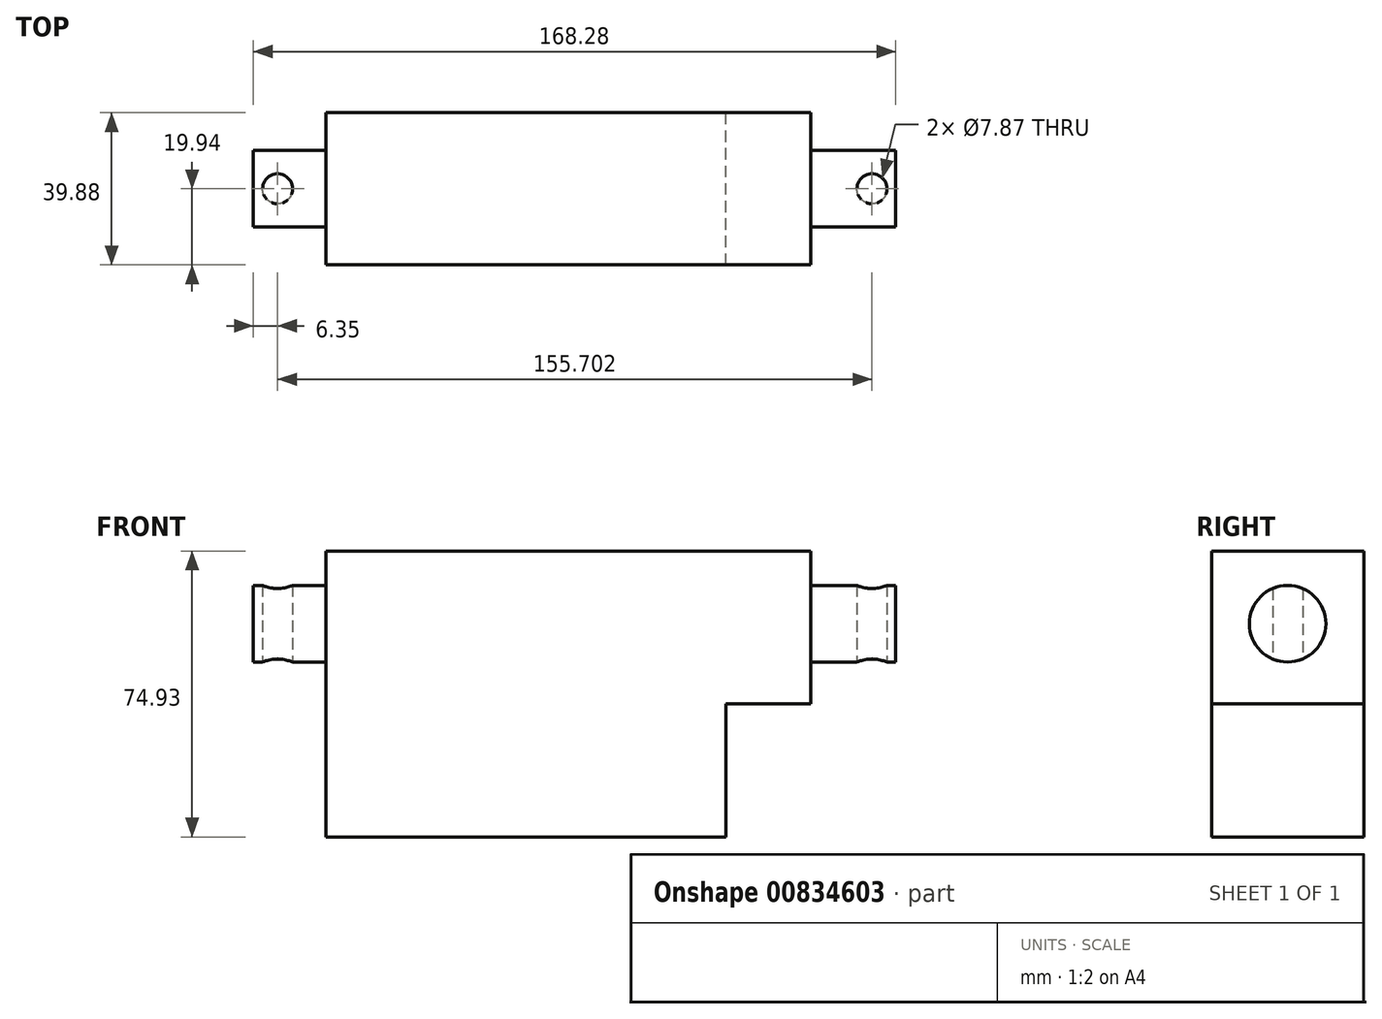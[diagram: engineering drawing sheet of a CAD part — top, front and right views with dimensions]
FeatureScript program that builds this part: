
annotation { "Feature Type Name" : "Feature", "Feature Type Description" : "" }
export const myFeature = defineFeature(function(context is Context, id is Id, definition is map)
    precondition{}
    {
        {
            var Q0;
            Q0=qCreatedBy(makeId("Right.planeOp"),FACE);
            var sketch = newSketch(context, id + "F0", { "sketchPlane" : qUnion([Q0])});
            skCircle(sketch, "E0", {"center": v(0, 0) * mm, "radius": 10.03 * mm});
            skSolve(sketch);
        }
        {
            var Q0;
            Q0 = qSketchRegion(id + "F0", true);
            extrude(context, id + "F1", {"entities" : qUnion([Q0]), "depth" : 168.27 * mm, "offsetDistance" : 25.4 * mm});
        }
        {
            var Q0;
            Q0=qCreatedBy(makeId("Right.planeOp"),FACE);
            cPlane(context, id + "F2", {"entities" : qUnion([Q0]), "cplaneType" : CPlaneType.OFFSET, "offset" : 19.05 * mm, "width" : 152.4 * mm, "height" : 152.4 * mm});
        }
        {
            var Q0;
            Q0=qCreatedBy(id+"F2.planeOp",FACE);
            var sketch = newSketch(context, id + "F3", { "sketchPlane" : qUnion([Q0])});
            skLineSegment(sketch, "E1.bottom", {"start": v(-19.94, 19.05) * mm, "end": v(19.94, 19.05) * mm});
            skLineSegment(sketch, "E1.top", {"start": v(-19.94, -55.88) * mm, "end": v(19.94, -55.88) * mm});
            skLineSegment(sketch, "E1.left", {"start": v(-19.94, 19.05) * mm, "end": v(-19.94, -55.88) * mm});
            skLineSegment(sketch, "E1.right", {"start": v(19.94, 19.05) * mm, "end": v(19.94, -55.88) * mm});
            skSolve(sketch);
        }
        {
            var Q0;
            Q0=makeQuery(id+"F3.imprint","IMPRINT",FACE,{"disambiguationData":[TD([[makeQuery(id+"F3.imprint","IMPRINT",EDGE,{"derivedFrom":sQuery(id+"F3.wireOp",EDGE,"E1.bottom")}),-1.0]])]});
            extrude(context, id + "F4", {"entities" : qUnion([Q0]), "operationType" : NewBodyOperationType.ADD, "depth" : 127 * mm, "offsetDistance" : 25.4 * mm});
        }
        {
            var Q0;
            Q0=makeQuery(id+"F4.opExtrude","CAP_FACE",FACE,{"disambiguationData":[OSD([sQuery(id+"F3.wireOp",EDGE,"E1.bottom"),sQuery(id+"F3.wireOp",EDGE,"E1.top"),sQuery(id+"F3.wireOp",EDGE,"E1.left"),sQuery(id+"F3.wireOp",EDGE,"E1.right")])],"isStart":false});
            var sketch = newSketch(context, id + "F5", { "sketchPlane" : qUnion([Q0])});
            skLineSegment(sketch, "E2.bottom", {"start": v(-19.94, -55.88) * mm, "end": v(19.94, -55.88) * mm});
            skLineSegment(sketch, "E2.top", {"start": v(-19.94, -20.96) * mm, "end": v(19.94, -20.96) * mm});
            skLineSegment(sketch, "E2.left", {"start": v(-19.94, -55.88) * mm, "end": v(-19.94, -20.96) * mm});
            skLineSegment(sketch, "E2.right", {"start": v(19.94, -55.88) * mm, "end": v(19.94, -20.96) * mm});
            skSolve(sketch);
        }
        {
            var Q0;
            Q0=makeQuery(id+"F5.imprint","IMPRINT",FACE,{"disambiguationData":[TD([[makeQuery(id+"F5.imprint","IMPRINT",EDGE,{"derivedFrom":sQuery(id+"F5.wireOp",EDGE,"E2.bottom")}),1.0]])]});
            extrude(context, id + "F6", {"entities" : qUnion([Q0]), "operationType" : NewBodyOperationType.REMOVE, "oppositeDirection" : true, "depth" : 22.22 * mm, "offsetDistance" : 25.4 * mm});
        }
        {
            var Q0;
            Q0=qCreatedBy(makeId("Top.planeOp"),FACE);
            var sketch = newSketch(context, id + "F7", { "sketchPlane" : qUnion([Q0])});
            skCircle(sketch, "E3", {"center": v(6.35, 0) * mm, "radius": 3.94 * mm});
            skCircle(sketch, "E4", {"center": v(162.05, 0) * mm, "radius": 3.94 * mm});
            skSolve(sketch);
        }
        {
            var Q0;
            Q0 = qSketchRegion(id + "F7", true);
            extrude(context, id + "F8", {"entities" : qUnion([Q0]), "operationType" : NewBodyOperationType.REMOVE, "endBound" : BoundingType.THROUGH_ALL, "depth" : 25.4 * mm, "offsetDistance" : 25.4 * mm, "hasSecondDirection" : true, "secondDirectionBound" : SecondDirectionBoundingType.THROUGH_ALL, "secondDirectionOppositeDirection" : true, "secondDirectionDepth" : 25.4 * mm});
        }
    });
